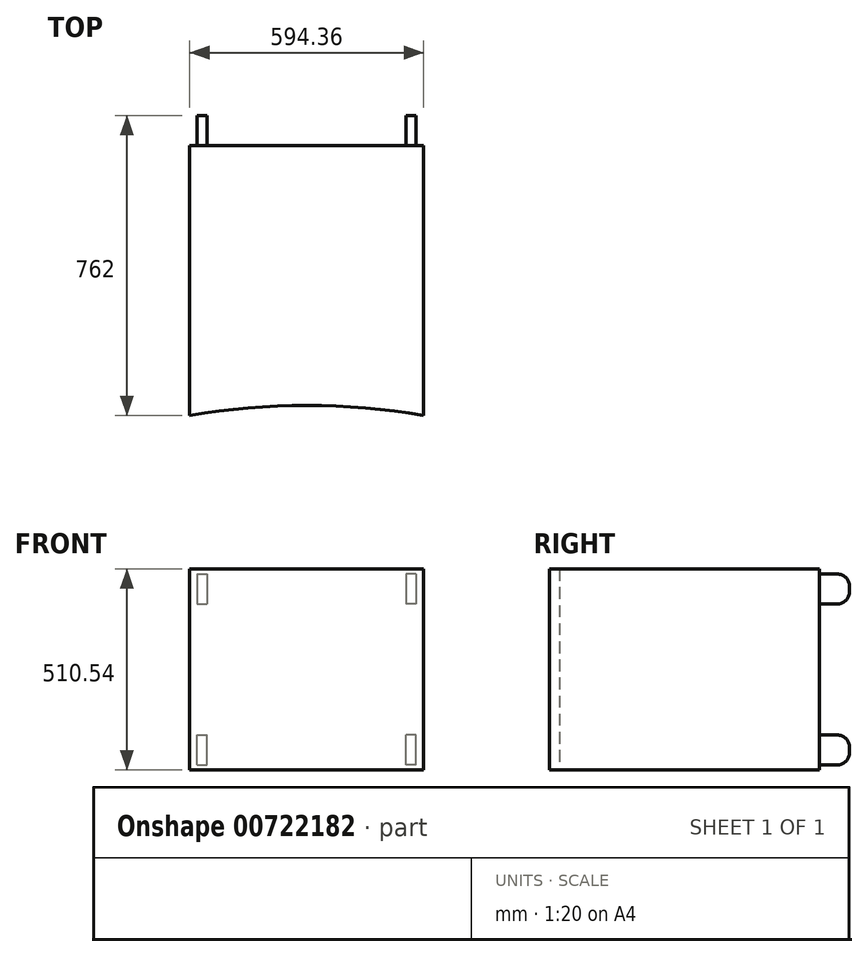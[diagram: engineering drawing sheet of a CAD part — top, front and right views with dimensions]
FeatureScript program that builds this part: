
annotation { "Feature Type Name" : "Feature", "Feature Type Description" : "" }
export const myFeature = defineFeature(function(context is Context, id is Id, definition is map)
    precondition{}
    {
        {
            var Q0;
            Q0=qCreatedBy(makeId("Top.planeOp"),FACE);
            var sketch = newSketch(context, id + "F0", { "sketchPlane" : qUnion([Q0])});
            skLineSegment(sketch, "E0", {"start": v(0, 685.8) * mm, "end": v(0, -158.39) * mm, "construction": true});
            skLineSegment(sketch, "E1.bottom", {"start": v(-297.18, 685.8) * mm, "end": v(297.18, 685.8) * mm});
            skLineSegment(sketch, "E1.left", {"start": v(-297.18, 685.8) * mm, "end": v(-297.18, 0) * mm});
            skLineSegment(sketch, "E1.right", {"start": v(297.18, 685.8) * mm, "end": v(297.18, 0) * mm});
            skLineSegment(sketch, "E2", {"start": v(-583.34, 0) * mm, "end": v(644.83, 0) * mm, "construction": true});
            skArc(sketch, "E3", {"start": v(297.18, 0) * mm, "mid": v(0, 25.4) * mm, "end": v(-297.18, 0) * mm});
            skPoint(sketch, "E4.positionSnap0", {"position": v(0, 25.4) * mm});
            skSolve(sketch);
        }
        {
            var Q0;
            Q0 = qSketchRegion(id + "F0", true);
            extrude(context, id + "F1", {"entities" : qUnion([Q0]), "depth" : 510.54 * mm, "offsetDistance" : 25.4 * mm});
        }
        {
            var Q0;
            Q0=makeQuery(id+"F1.opExtrude","SWEPT_FACE",FACE,{"disambiguationData":[OSD([sQuery(id+"F0.wireOp",EDGE,"E1.bottom")])]});
            var sketch = newSketch(context, id + "F2", { "sketchPlane" : qUnion([Q0])});
            skLineSegment(sketch, "E5", {"start": v(0, 0) * mm, "end": v(0, 652.77) * mm, "construction": true});
            skLineSegment(sketch, "E6", {"start": v(-297.18, 255.27) * mm, "end": v(465.88, 255.27) * mm, "construction": true});
            skLineSegment(sketch, "E7.bottom", {"start": v(-278.13, 497.84) * mm, "end": v(-252.73, 497.84) * mm});
            skLineSegment(sketch, "E7.top", {"start": v(-278.13, 421.64) * mm, "end": v(-252.73, 421.64) * mm});
            skLineSegment(sketch, "E7.left", {"start": v(-278.13, 497.84) * mm, "end": v(-278.13, 421.64) * mm});
            skLineSegment(sketch, "E7.right", {"start": v(-252.73, 497.84) * mm, "end": v(-252.73, 421.64) * mm});
            skLineSegment(sketch, "E8.MirrorCS", {"start": v(252.73, 497.84) * mm, "end": v(252.73, 421.64) * mm});
            skLineSegment(sketch, "E9.MirrorCS", {"start": v(278.13, 497.84) * mm, "end": v(278.13, 421.64) * mm});
            skLineSegment(sketch, "E10.MirrorCS", {"start": v(278.13, 421.64) * mm, "end": v(252.73, 421.64) * mm});
            skLineSegment(sketch, "E11.MirrorCS", {"start": v(278.13, 497.84) * mm, "end": v(252.73, 497.84) * mm});
            skLineSegment(sketch, "E12.MirrorCS", {"start": v(-278.13, 88.9) * mm, "end": v(-252.73, 88.9) * mm});
            skLineSegment(sketch, "E13.MirrorCS", {"start": v(-278.13, 12.7) * mm, "end": v(-278.13, 88.9) * mm});
            skLineSegment(sketch, "E14.MirrorCS", {"start": v(-252.73, 12.7) * mm, "end": v(-252.73, 88.9) * mm});
            skLineSegment(sketch, "E15.MirrorCS", {"start": v(-278.13, 12.7) * mm, "end": v(-252.73, 12.7) * mm});
            skLineSegment(sketch, "E16.MirrorCS", {"start": v(278.13, 12.7) * mm, "end": v(278.13, 88.9) * mm});
            skLineSegment(sketch, "E17.MirrorCS", {"start": v(278.13, 88.9) * mm, "end": v(252.73, 88.9) * mm});
            skLineSegment(sketch, "E18.MirrorCS", {"start": v(278.13, 12.7) * mm, "end": v(252.73, 12.7) * mm});
            skLineSegment(sketch, "E19.MirrorCS", {"start": v(252.73, 12.7) * mm, "end": v(252.73, 88.9) * mm});
            skSolve(sketch);
        }
        {
            var Q0;
            Q0 = qSketchRegion(id + "F2", true);
            extrude(context, id + "F3", {"entities" : qUnion([Q0]), "operationType" : NewBodyOperationType.ADD, "depth" : 76.2 * mm, "offsetDistance" : 25.4 * mm});
        }
        {
            var Q0;
            Q0=makeQuery(id+"F3.opExtrude","CAP_EDGE",EDGE,{"disambiguationData":[OSD([sQuery(id+"F2.wireOp",EDGE,"E7.bottom")])],"isStart":false});
            var Q1;
            Q1=makeQuery(id+"F3.opExtrude","CAP_EDGE",EDGE,{"disambiguationData":[OSD([sQuery(id+"F2.wireOp",EDGE,"E7.top")])],"isStart":false});
            var Q2;
            Q2=makeQuery(id+"F3.opExtrude","CAP_EDGE",EDGE,{"disambiguationData":[OSD([sQuery(id+"F2.wireOp",EDGE,"E12.MirrorCS")])],"isStart":false});
            var Q3;
            Q3=makeQuery(id+"F3.opExtrude","CAP_EDGE",EDGE,{"disambiguationData":[OSD([sQuery(id+"F2.wireOp",EDGE,"E18.MirrorCS")])],"isStart":false});
            var Q4;
            Q4=makeQuery(id+"F3.opExtrude","CAP_EDGE",EDGE,{"disambiguationData":[OSD([sQuery(id+"F2.wireOp",EDGE,"E17.MirrorCS")])],"isStart":false});
            var Q5;
            Q5=makeQuery(id+"F3.opExtrude","CAP_EDGE",EDGE,{"disambiguationData":[OSD([sQuery(id+"F2.wireOp",EDGE,"E10.MirrorCS")])],"isStart":false});
            var Q6;
            Q6=makeQuery(id+"F3.opExtrude","CAP_EDGE",EDGE,{"disambiguationData":[OSD([sQuery(id+"F2.wireOp",EDGE,"E11.MirrorCS")])],"isStart":false});
            var Q7;
            Q7=makeQuery(id+"F3.opExtrude","CAP_EDGE",EDGE,{"disambiguationData":[OSD([sQuery(id+"F2.wireOp",EDGE,"E15.MirrorCS")])],"isStart":false});
            fillet(context, id + "F4", {"entities" : qUnion([Q0, Q1, Q2, Q3, Q4, Q5, Q6, Q7]), "radius" : 31.75 * mm, "tangentPropagation" : true, "allowEdgeOverflow" : false});
        }
    });
